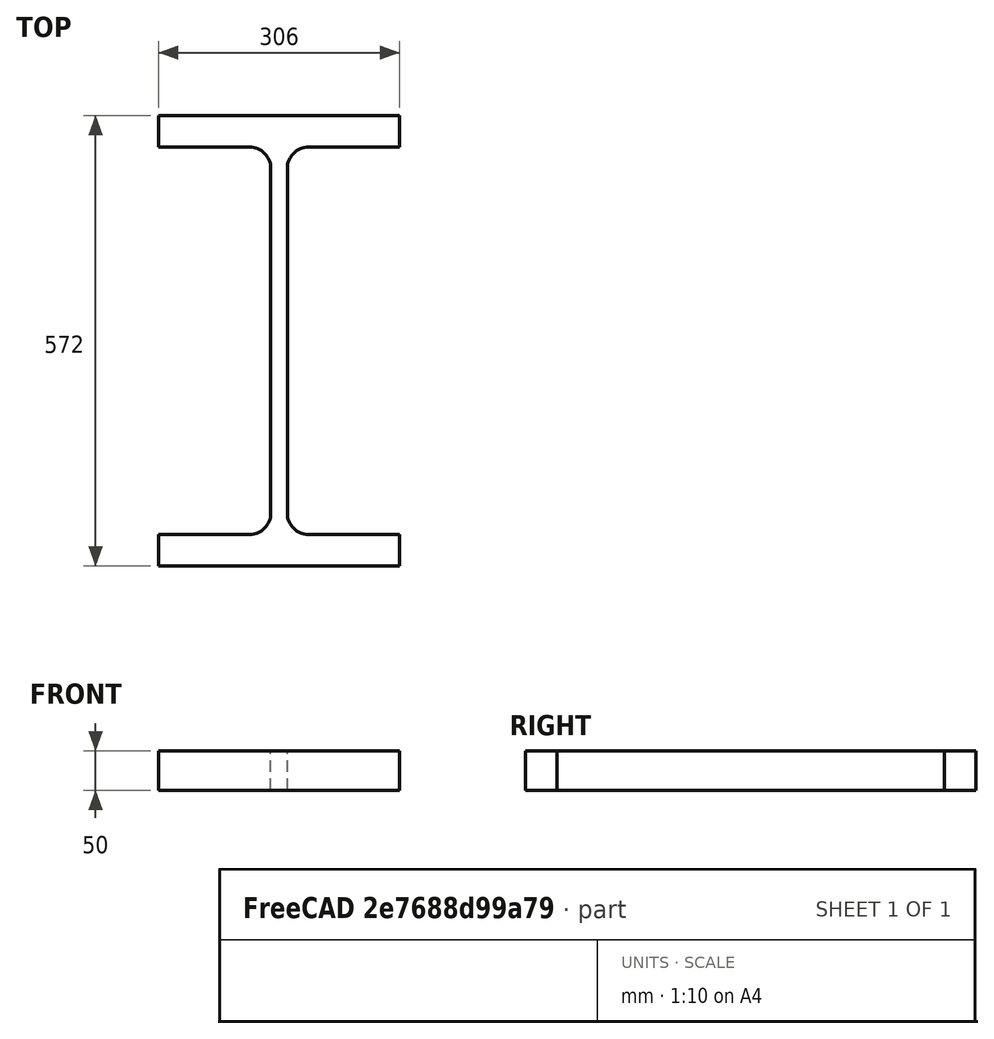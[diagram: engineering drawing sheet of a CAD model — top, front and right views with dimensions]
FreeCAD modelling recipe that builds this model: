
FCSTD DOCUMENT  (FreeCAD 0.15R4671 (Git))
Label: HE-M-Profile 550 DIN1025-4 S235JR
License: All rights reserved
LicenseURL: http://en.wikipedia.org/wiki/All_rights_reserved
objects: Sketcher::SketchObject×1, Part::Extrusion×1
note: 2 computed .brp shape members not serialized (recipe doc carries the construction recipe); baked Part::Feature solids carry a one-line shape summary decoded from their .brp

FEATURE [Sketcher::SketchObject] Sketch
  sketch-geometry (16):
    g0: LineSegment StartX=10.5 StartY=-219 StartZ=0 EndX=10.5 EndY=219 EndZ=0
    g1: LineSegment StartX=37.5 StartY=246 StartZ=0 EndX=153 EndY=246 EndZ=0
    g2: LineSegment StartX=153 StartY=246 StartZ=0 EndX=153 EndY=286 EndZ=0
    g3: LineSegment StartX=153 StartY=286 StartZ=0 EndX=-153 EndY=286 EndZ=0
    g4: LineSegment StartX=-153 StartY=286 StartZ=0 EndX=-153 EndY=246 EndZ=0
    g5: LineSegment StartX=-153 StartY=246 StartZ=0 EndX=-37.5 EndY=246 EndZ=0
    g6: LineSegment StartX=-10.5 StartY=219 StartZ=0 EndX=-10.5 EndY=-219 EndZ=0
    g7: LineSegment StartX=-37.5 StartY=-246 StartZ=0 EndX=-153 EndY=-246 EndZ=0
    g8: LineSegment StartX=-153 StartY=-246 StartZ=0 EndX=-153 EndY=-286 EndZ=0
    g9: LineSegment StartX=-153 StartY=-286 StartZ=0 EndX=153 EndY=-286 EndZ=0
    g10: LineSegment StartX=153 StartY=-286 StartZ=0 EndX=153 EndY=-246 EndZ=0
    g11: LineSegment StartX=153 StartY=-246 StartZ=0 EndX=37.5 EndY=-246 EndZ=0
    g12: ArcOfCircle CenterX=37.5 CenterY=219 CenterZ=0 NormalX=0 NormalY=0 NormalZ=1 Radius=27 StartAngle=1.5708 EndAngle=3.14159
    g13: ArcOfCircle CenterX=37.5 CenterY=-219 CenterZ=0 NormalX=0 NormalY=0 NormalZ=1 Radius=27 StartAngle=3.14159 EndAngle=4.71239
    g14: ArcOfCircle CenterX=-37.5 CenterY=219 CenterZ=0 NormalX=0 NormalY=0 NormalZ=1 Radius=27 StartAngle=0 EndAngle=1.5708
    g15: ArcOfCircle CenterX=-37.5 CenterY=-219 CenterZ=0 NormalX=0 NormalY=0 NormalZ=1 Radius=27 StartAngle=4.71239 EndAngle=6.28319
  constraints (42):
    c: Vertical(g0)
    c: Coincident(g2,g1)
    c: Vertical(g2)
    c: Coincident(g3,g2)
    c: Coincident(g4,g3)
    c: Vertical(g4)
    c: Coincident(g5,g4)
    c: Horizontal(g5)
    c: Vertical(g6)
    c: Horizontal(g7)
    c: Coincident(g8,g7)
    c: Vertical(g8)
    c: Coincident(g9,g8)
    c: Horizontal(g9)
    c: Coincident(g10,g9)
    c: Vertical(g10)
    c: Coincident(g11,g10)
    c: Horizontal(g11)
    c: Tangent(g1,g12) = 1.5708
    c: Tangent(g0,g12) = 1.5708
    c: Tangent(g0,g13) = 1.5708
    c: Tangent(g11,g13) = 1.5708
    c: Tangent(g5,g14) = 1.5708
    c: Tangent(g6,g14) = 1.5708
    c: Tangent(g6,g15) = 1.5708
    c: Tangent(g7,g15) = 1.5708
    c: Equal(g3,g9)
    c: Equal(g2,g4)
    c: Equal(g4,g8)
    c: Equal(g8,g10)
    c: Equal(g12,g14)
    c: Equal(g14,g15)
    c: Equal(g15,g13)
    c: Symmetric(g2,g3,g-2)
    c: Symmetric(g9,g8,g-2)
    c: Symmetric(g0,g6,g-2)
    c: Symmetric(g2,g9,g-1)
    c: DistanceY(g2,g9) = -572
    c: DistanceX(g3) = -306
    c: DistanceX(g0,g6) = -21
    c: DistanceY(g2) = 40
    c: Radius(g12) = 27
FEATURE [Part::Extrusion] Extrude  label="HE-M-Profile 550 DIN1025-4 S235JR"
  Base = -> Sketch
  Dir = (0,0,50)
  Solid = true
